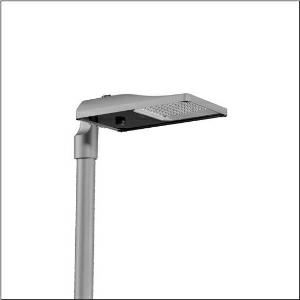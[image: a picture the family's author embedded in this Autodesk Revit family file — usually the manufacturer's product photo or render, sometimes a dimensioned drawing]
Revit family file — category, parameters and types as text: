
# Revit family: streetlight_sl_31_midi___st0_5a_5xh7b31t08qa_33e3
name_source: partatom
category: Lighting Fixtures
units: mm (PartAtom-declared; Revit-internal decimal feet)

## family parameters
Cut with Voids When Loaded = No
Host = Face
Light Source = No
Part Type = Normal
Room Calculation Point = No
Round Connector Dimension = Use Diameter
Shared = No

## types (1)
- --- (1 x LED, 24430 lm, 163.3 W, 3000K)
    Apparent Load = 163 VA
    CIE Flux Codes = 43 76 97 100 100
    Color Rendering = 70
    Color Temperature = 3000K
    Default Elevation = 1800 mm
    Description = Streetlight SL 31 midi D4i, Desk-Remote mast luminaire for post-top, side-entry; light control with lens of PMMA; light distribution: ST0.5a, direct asymmetric distribution, for standard-compliant lighting for roads and squares; LED: luminous flux: 24.430lm, light colour: 730, colour temperature: 3000K; luminous efficacy: 149,6lm/W; control: pre-setting: logarithmic dimming characteristic, flexible luminous flux parameterisation, time-dependent luminous flux control, constant luminous flux control, power reduction, intelligent temperature release in ECG and LED module, overheat protection; luminaire housing, of diecast aluminium, SITECO metallic grey (DB 702S), corrosivity category C5 high according to DIN EN ISO 12944; cover of toughened safety glass, transparent, opened without tools; mast flange of diecast aluminium, SITECO metallic grey (DB 702S), spigot size: 76/60mm, mast flange included unmounted; cable length: 14,5m, connection cable pre-assembled; mains connection: 220..240V, AC, 50/60Hz; power consumption (at start of service life): 163,3W / (at end of service life): 178,2W / (with reduced operation 50%): 73W; protection rating (complete): IP66; insulation class (complete): insulation class II (safety insulation); impact resistance: IK09; certification: CE, ENEC, ENEC+, VDE, UKCA, ZD4i; permissible operating ambient temperature for outdoor applications: -40..+50°C; packaging unit: 1 piece

Light Distribution: ST0.5a
    Height = 79 mm
    Lamp = 1 x LED
    Lamp Light Flux = 24430 lm
    Lamp Power = 163.3 W
    Lamp count = 1
    Length = 577 mm
    Luminous efficacy = 150 lm/W
    Manufacturer = Siteco
    ModVariant = No
    Model = 5XH7B31T08QA
    Number of Poles = 1
    OnlyDefault = Yes
    Power Factor = 1
    Product Name = Streetlight SL 31 midi | ST0.5a
    Product group = mast luminaire | pylon top
    ProductGroupID = 6100
    Protection Class = Protection class II
    Protection Degree = IP 66
    RLX_Detail_Level = 1
    RLX_Emergency_Light_Flux = 0 lm
    RLX_Emergency_Type = 0
    RLX_Emergency_Type_DB = No
    RlxData = <blob elided: 54305 chars, md5=765e0e7e>
    Socket = socket
    Standby Power = 0 W
    System Light Flux = 24430 lm
    System Power = 163 W
    Type Comments = factory setting: luminous flux: 100 % | dim-lin: 254 | 865 mA
    Type Image = l_1300321.jpg
    URL = http://relux.com
    VarID = @adj_064077
    Voltage = 0 V
    Weight = 0.00 kg
    Width = 362 mm

## geometry (parser evidence)
native form markers: Blend x4, Sweep x12
no freeform markers — native parametric forms only
